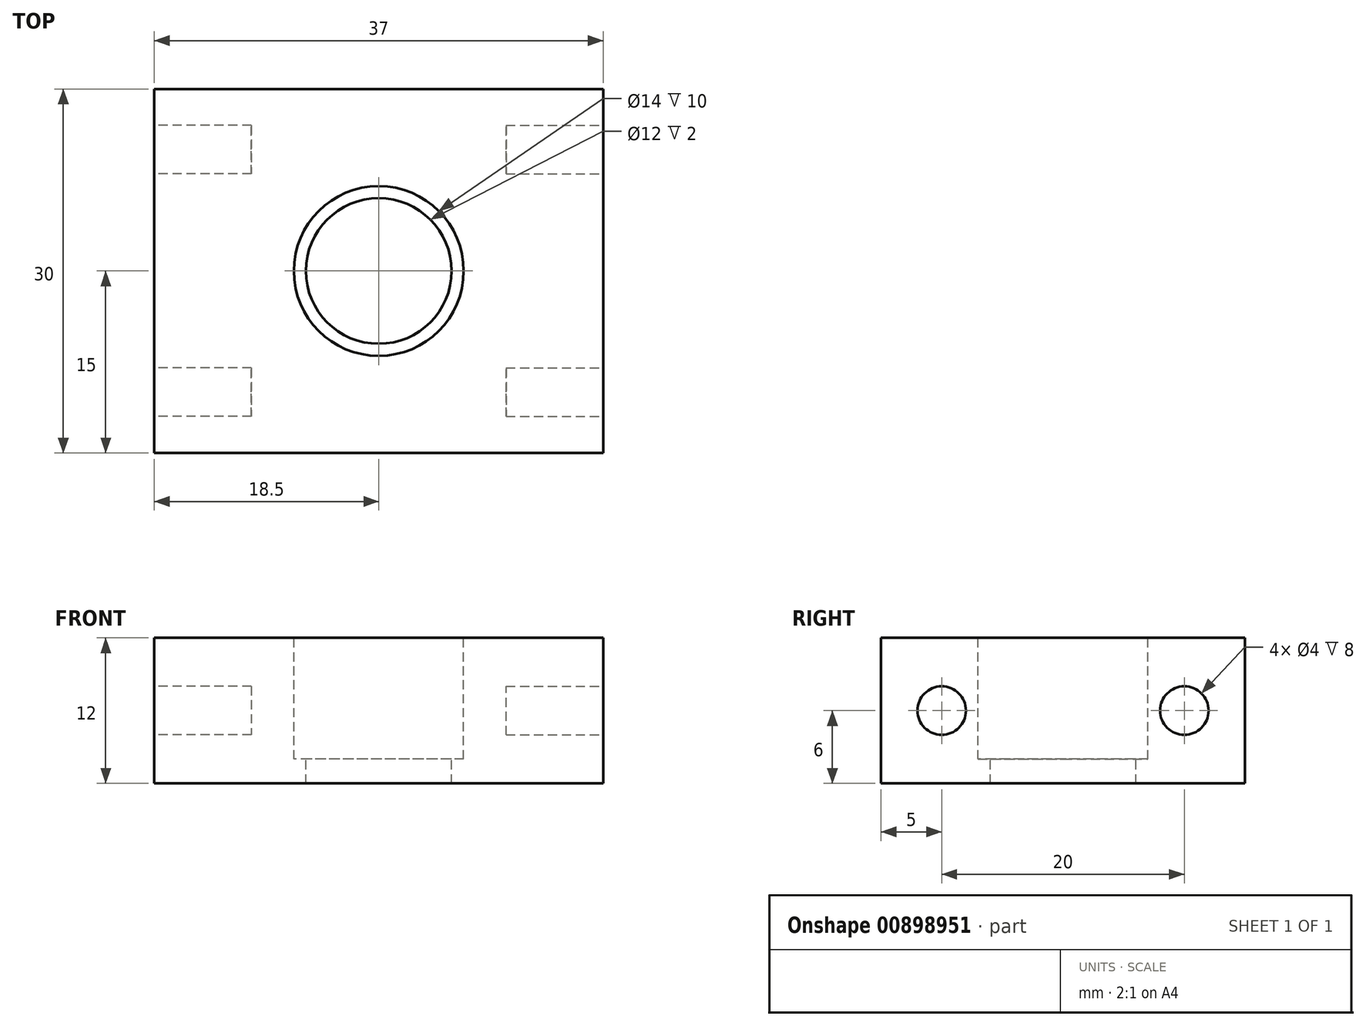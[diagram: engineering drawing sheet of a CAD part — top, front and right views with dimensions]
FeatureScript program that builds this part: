
annotation { "Feature Type Name" : "Feature", "Feature Type Description" : "" }
export const myFeature = defineFeature(function(context is Context, id is Id, definition is map)
    precondition{}
    {
        {
            var Q0;
            Q0=qCreatedBy(makeId("Top.planeOp"),FACE);
            var sketch = newSketch(context, id + "F0", { "sketchPlane" : qUnion([Q0])});
            skLineSegment(sketch, "E0.bottom", {"start": v(0, 0) * mm, "end": v(37, 0) * mm});
            skLineSegment(sketch, "E0.top", {"start": v(0, -30) * mm, "end": v(37, -30) * mm});
            skLineSegment(sketch, "E0.left", {"start": v(0, 0) * mm, "end": v(0, -30) * mm});
            skLineSegment(sketch, "E0.right", {"start": v(37, 0) * mm, "end": v(37, -30) * mm});
            skSolve(sketch);
        }
        {
            var Q0;
            Q0 = qSketchRegion(id + "F0", true);
            extrude(context, id + "F1", {"entities" : qUnion([Q0]), "depth" : 12 * mm, "offsetDistance" : 25 * mm});
        }
        {
            var Q0;
            Q0=makeQuery(id+"F1.opExtrude","CAP_FACE",FACE,{"disambiguationData":[OSD([sQuery(id+"F0.wireOp",EDGE,"E0.bottom"),sQuery(id+"F0.wireOp",EDGE,"E0.top"),sQuery(id+"F0.wireOp",EDGE,"E0.left"),sQuery(id+"F0.wireOp",EDGE,"E0.right")])],"isStart":false});
            var sketch = newSketch(context, id + "F2", { "sketchPlane" : qUnion([Q0])});
            skCircle(sketch, "E1", {"center": v(18.5, -15) * mm, "radius": 7 * mm});
            skPoint(sketch, "E1.centerSnap0", {"position": v(0, -15) * mm});
            skSolve(sketch);
        }
        {
            var Q0;
            Q0 = qSketchRegion(id + "F2", true);
            extrude(context, id + "F3", {"entities" : qUnion([Q0]), "operationType" : NewBodyOperationType.REMOVE, "oppositeDirection" : true, "depth" : 10 * mm, "offsetDistance" : 25 * mm});
        }
        {
            var Q0;
            Q0=makeQuery(id+"F1.opExtrude","SWEPT_FACE",FACE,{"disambiguationData":[OSD([sQuery(id+"F0.wireOp",EDGE,"E0.right")])]});
            var sketch = newSketch(context, id + "F4", { "sketchPlane" : qUnion([Q0])});
            skCircle(sketch, "E2", {"center": v(-5, 6) * mm, "radius": 2 * mm});
            skCircle(sketch, "E3", {"center": v(-25, 6) * mm, "radius": 2 * mm});
            skSolve(sketch);
        }
        {
            var Q0;
            Q0 = qSketchRegion(id + "F4", true);
            extrude(context, id + "F5", {"entities" : qUnion([Q0]), "operationType" : NewBodyOperationType.REMOVE, "oppositeDirection" : true, "depth" : 8 * mm, "offsetDistance" : 25 * mm});
        }
        {
            var Q0;
            Q0=makeQuery(id+"F1.opExtrude","SWEPT_FACE",FACE,{"disambiguationData":[OSD([sQuery(id+"F0.wireOp",EDGE,"E0.left")])]});
            var sketch = newSketch(context, id + "F6", { "sketchPlane" : qUnion([Q0])});
            skCircle(sketch, "E4", {"center": v(25, 6) * mm, "radius": 2 * mm});
            skCircle(sketch, "E5", {"center": v(5, 6) * mm, "radius": 2 * mm});
            skSolve(sketch);
        }
        {
            var Q0;
            Q0 = qSketchRegion(id + "F6", true);
            extrude(context, id + "F7", {"entities" : qUnion([Q0]), "operationType" : NewBodyOperationType.REMOVE, "oppositeDirection" : true, "depth" : 8 * mm, "offsetDistance" : 25 * mm});
        }
        {
            var Q0;
            Q0=makeQuery(id+"F3.boolean.opBoolean","COPY",FACE,{"derivedFrom":makeQuery(id+"F3.opExtrude","CAP_FACE",FACE,{"disambiguationData":[OSD([sQuery(id+"F2.wireOp",EDGE,"E1")])],"isStart":false})});
            var sketch = newSketch(context, id + "F8", { "sketchPlane" : qUnion([Q0])});
            skCircle(sketch, "E6", {"center": v(18.5, -15) * mm, "radius": 6 * mm});
            skSolve(sketch);
        }
        {
            var Q0;
            Q0 = qSketchRegion(id + "F8", true);
            extrude(context, id + "F9", {"entities" : qUnion([Q0]), "operationType" : NewBodyOperationType.REMOVE, "oppositeDirection" : true, "depth" : 25 * mm, "offsetDistance" : 25 * mm});
        }
    });
